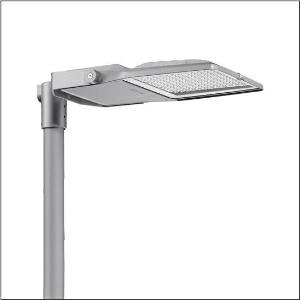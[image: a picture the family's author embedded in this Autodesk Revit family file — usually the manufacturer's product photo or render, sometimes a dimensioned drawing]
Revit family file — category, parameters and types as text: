
# Revit family: floodlight_fl_21_iq_midi___pl64_5xa7781e4e3a_69c6
name_source: partatom
category: Lighting Fixtures
units: mm (PartAtom-declared; Revit-internal decimal feet)

## family parameters
Cut with Voids When Loaded = No
Host = Face
Light Source = No
Part Type = Normal
Room Calculation Point = No
Round Connector Dimension = Use Diameter
Shared = No

## types (1)
- --- (1 x LED, 27050 lm, 208.1 W, 4000K)
    Apparent Load = 208 VA
    CIE Flux Codes = 28 80 98 100 100
    Color Rendering = 70
    Color Temperature = 4000K
    Default Elevation = 1800 mm
    Description = Floodlight FL 21 iQ midi, floodlight, primary light control with lens, of PMMA, primary optical cover: protective disc, of toughened safety glass, transparent, light distribution: PL64, light emission: direct distribution, installation type: surface-mounted, LED, High Power LED, rated luminous flux: 27.050lm, luminous efficacy: 130lm/W, light colour: 740, colour temperature: 4000K, control gear: ECG iQ, control: optimised constant luminous flux control (CLO 2.0), Desk-Remote (wireless, voltage-free reading and setting of iQ features in the workshop via application-optimized NFC function/RFID function), Light-Fading, Smart-Wire, Night-Set, Lumen-Switch, Temp-Guard, Auto-Match, with terminal, 6-pole, mains connection: 220..240V, AC, 50/60Hz, start of lifetime: 208W, end of service life: 227W, reduction: 90W, luminaire housing, of diecast aluminium, powder-coated, Siteco® metallic grey (DB 702S), corrosivity category C5 mid according to DIN EN ISO 12944, sealing non-destructively replaceable, please order mast flange separately, mast bracket, of steel, galvanised, powder-coated, Siteco® metallic grey (DB 702S), protection rating (complete): IP66, insulation class (complete): insulation class II (safety insulation), certification: CE, ENEC, VDE, protection symbol: D, impact resistance: IK08, permissible operating ambient temperature: -40..+40°C, permissible operating ambient temperature for outdoor applications: -40..+50°C, standard: DIN EN 12944, LABS conformity tested according to VDMA 24364:2018-05, packaging unit: 1 piece

Light Distribution: PL64
    Height = 76 mm
    Lamp = 1 x LED
    Lamp Light Flux = 27050 lm
    Lamp Power = 208.1 W
    Lamp count = 1
    Length = 657 mm
    Luminous efficacy = 130 lm/W
    Manufacturer = Siteco
    ModVariant = No
    Model = 5XA7781E4E3A
    Number of Poles = 1
    OnlyDefault = Yes
    Power Factor = 1
    Product Name = Floodlight FL 21 iQ midi | PL64
    Product group = floodlight | pylon annexe
    ProductGroupID = 6200
    Protection Class = Protection class II
    Protection Degree = IP 66
    RLX_Detail_Level = 1
    RLX_Emergency_Light_Flux = 0 lm
    RLX_Emergency_Type = 0
    RLX_Emergency_Type_DB = No
    RlxData = <blob elided: 153561 chars, md5=2a8309cb>
    Socket = socket
    Standby Power = 0 W
    System Light Flux = 27050 lm
    System Power = 208 W
    Type Comments = factory setting: luminous flux: 100 % | dim-lin: 254 | 710 mA
    Type Image = l_1007123.jpg
    URL = http://relux.com
    VarID = @adj_076057
    Voltage = 0 V
    Weight = 0.00 kg
    Width = 442 mm

## geometry (parser evidence)
native form markers: Blend x4, Sweep x15
no freeform markers — native parametric forms only
